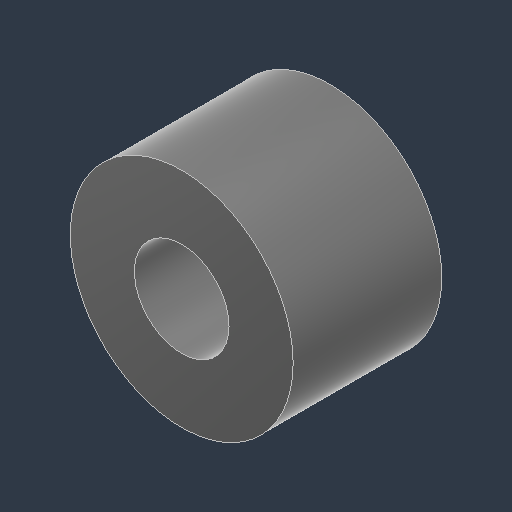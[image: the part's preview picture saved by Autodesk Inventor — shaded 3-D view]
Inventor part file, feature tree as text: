
AUTODESK INVENTOR PART (.ipt)
format: ipt  version: 2024.3 (Build 283343000, 343)  size: 114,688 bytes
history: native  units: in
note: dims shown in document units (in); Inventor stores cm internally (conversion verified against a paired STEP export)
features: extrude x1, sketch x1
ambient origin geometry x8: Origin, YZ Plane, XZ Plane, XY Plane, X Axis, Y Axis, Z Axis, Center Point
bodies: Solid1 (feature_tree)
feature tree (2):
  extrude  "Extrusion1"  Depth=0.5in
  sketch  "Sketch1"  dims[d0=0.3185in d1=0.75in d2=0.5in d3=0.0in]
